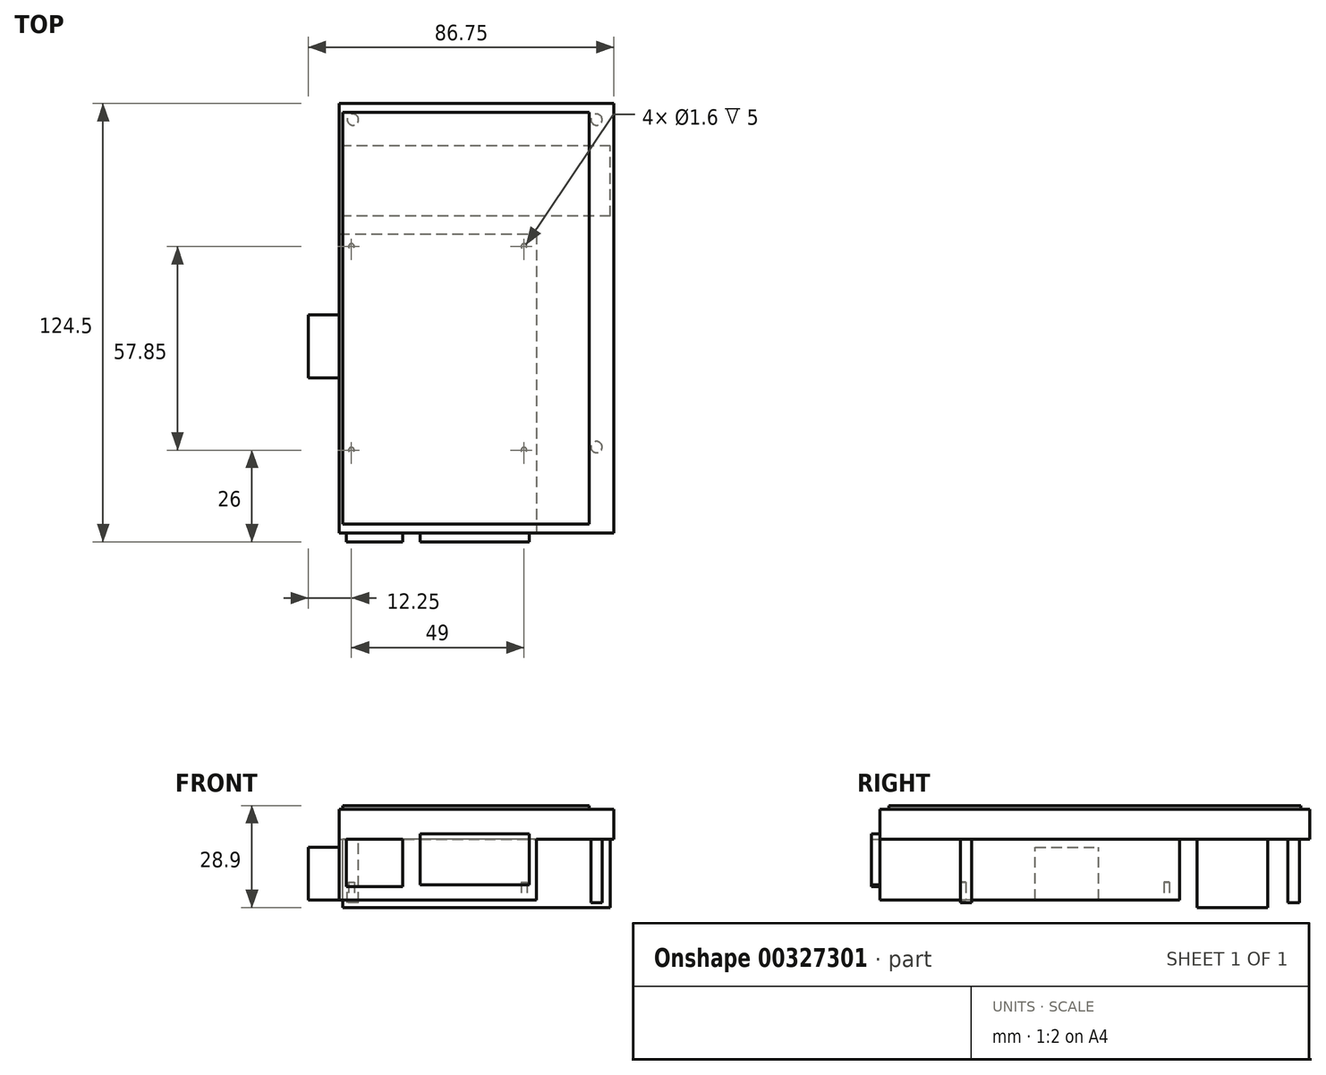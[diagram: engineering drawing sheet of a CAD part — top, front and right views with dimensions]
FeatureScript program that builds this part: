
annotation { "Feature Type Name" : "Feature", "Feature Type Description" : "" }
export const myFeature = defineFeature(function(context is Context, id is Id, definition is map)
    precondition{}
    {
        {
            var Q0;
            Q0=qCreatedBy(makeId("Top.planeOp"),FACE);
            var sketch = newSketch(context, id + "F0", { "sketchPlane" : qUnion([Q0])});
            skLineSegment(sketch, "E0.bottom", {"start": v(-39, -61) * mm, "end": v(39, -61) * mm});
            skLineSegment(sketch, "E0.top", {"start": v(-39, 61) * mm, "end": v(39, 61) * mm});
            skLineSegment(sketch, "E0.left", {"start": v(-39, -61) * mm, "end": v(-39, 61) * mm});
            skLineSegment(sketch, "E0.right", {"start": v(39, -61) * mm, "end": v(39, 61) * mm});
            skPoint(sketch, "E0.middle", {"position": v(0, 0) * mm});
            skSolve(sketch);
        }
        {
            var Q0;
            Q0 = qSketchRegion(id + "F0", true);
            extrude(context, id + "F1", {"entities" : qUnion([Q0]), "depth" : 8.5 * mm});
        }
        {
            var Q0;
            Q0=makeQuery(id+"F1.opExtrude","CAP_FACE",FACE,{"disambiguationData":[OSD([sQuery(id+"F0.wireOp",EDGE,"E0.bottom"),sQuery(id+"F0.wireOp",EDGE,"E0.top"),sQuery(id+"F0.wireOp",EDGE,"E0.left"),sQuery(id+"F0.wireOp",EDGE,"E0.right")])],"isStart":false});
            var sketch = newSketch(context, id + "F2", { "sketchPlane" : qUnion([Q0])});
            skLineSegment(sketch, "E1.bottom", {"start": v(-38, 58.5) * mm, "end": v(32, 58.5) * mm});
            skLineSegment(sketch, "E1.top", {"start": v(-38, -58.5) * mm, "end": v(32, -58.5) * mm});
            skLineSegment(sketch, "E1.left", {"start": v(-38, 58.5) * mm, "end": v(-38, -58.5) * mm});
            skLineSegment(sketch, "E1.right", {"start": v(32, 58.5) * mm, "end": v(32, -58.5) * mm});
            skPoint(sketch, "E1.middle", {"position": v(-3, 0) * mm});
            skPoint(sketch, "E1.middle.positionSnap0", {"position": v(-39, 0) * mm});
            skPoint(sketch, "E1.centerSnap0", {"position": v(-39, 0) * mm});
            skSolve(sketch);
        }
        {
            var Q0;
            Q0 = qSketchRegion(id + "F2", true);
            extrude(context, id + "F3", {"entities" : qUnion([Q0]), "operationType" : NewBodyOperationType.ADD, "depth" : 1 * mm});
        }
        {
            var Q0;
            Q0=makeQuery(id+"F1.opExtrude","CAP_FACE",FACE,{"disambiguationData":[OSD([sQuery(id+"F0.wireOp",EDGE,"E0.bottom"),sQuery(id+"F0.wireOp",EDGE,"E0.top"),sQuery(id+"F0.wireOp",EDGE,"E0.left"),sQuery(id+"F0.wireOp",EDGE,"E0.right")])],"isStart":true});
            var sketch = newSketch(context, id + "F4", { "sketchPlane" : qUnion([Q0])});
            skLineSegment(sketch, "E2.bottom", {"start": v(-39, -24) * mm, "end": v(17, -24) * mm});
            skLineSegment(sketch, "E2.top", {"start": v(-39, 61) * mm, "end": v(17, 61) * mm});
            skLineSegment(sketch, "E2.left", {"start": v(-39, -24) * mm, "end": v(-39, 61) * mm});
            skLineSegment(sketch, "E2.right", {"start": v(17, -24) * mm, "end": v(17, 61) * mm});
            skPoint(sketch, "E2.middle", {"position": v(-11, 18.5) * mm});
            skSolve(sketch);
        }
        {
            var Q0;
            Q0 = qSketchRegion(id + "F4", true);
            extrude(context, id + "F5", {"entities" : qUnion([Q0]), "operationType" : NewBodyOperationType.ADD, "depth" : 17.25 * mm});
        }
        {
            var Q0;
            Q0=makeQuery(id+"F5.boolean.opBoolean","MERGE",FACE,{"derivedFrom":[makeQuery(id+"F1.opExtrude","SWEPT_FACE",FACE,{"disambiguationData":[OSD([sQuery(id+"F0.wireOp",EDGE,"E0.left")])]}),makeQuery(id+"F5.opExtrude","SWEPT_FACE",FACE,{"disambiguationData":[OSD([sQuery(id+"F4.wireOp",EDGE,"E2.left")])]})]});
            var sketch = newSketch(context, id + "F6", { "sketchPlane" : qUnion([Q0])});
            skLineSegment(sketch, "E3.bottom", {"start": v(17, -17.25) * mm, "end": v(-1, -17.25) * mm});
            skLineSegment(sketch, "E3.top", {"start": v(17, -2.25) * mm, "end": v(-1, -2.25) * mm});
            skLineSegment(sketch, "E3.left", {"start": v(17, -17.25) * mm, "end": v(17, -2.25) * mm});
            skLineSegment(sketch, "E3.right", {"start": v(-1, -17.25) * mm, "end": v(-1, -2.25) * mm});
            skSolve(sketch);
        }
        {
            var Q0;
            Q0 = qSketchRegion(id + "F6", true);
            extrude(context, id + "F7", {"entities" : qUnion([Q0]), "operationType" : NewBodyOperationType.ADD, "depth" : 8.75 * mm});
        }
        {
            var Q0;
            Q0=makeQuery(id+"F5.boolean.opBoolean","MERGE",FACE,{"derivedFrom":[makeQuery(id+"F1.opExtrude","SWEPT_FACE",FACE,{"disambiguationData":[OSD([sQuery(id+"F0.wireOp",EDGE,"E0.bottom")])]}),makeQuery(id+"F5.opExtrude","SWEPT_FACE",FACE,{"disambiguationData":[OSD([sQuery(id+"F4.wireOp",EDGE,"E2.top")])]})]});
            var sketch = newSketch(context, id + "F8", { "sketchPlane" : qUnion([Q0])});
            skLineSegment(sketch, "E4.bottom", {"start": v(-36.9, 0) * mm, "end": v(-20.9, 0) * mm});
            skLineSegment(sketch, "E4.top", {"start": v(-36.9, -13.5) * mm, "end": v(-20.9, -13.5) * mm});
            skLineSegment(sketch, "E4.left", {"start": v(-36.9, 0) * mm, "end": v(-36.9, -13.5) * mm});
            skLineSegment(sketch, "E4.right", {"start": v(-20.9, 0) * mm, "end": v(-20.9, -13.5) * mm});
            skPoint(sketch, "E4.middle", {"position": v(-28.9, -6.75) * mm});
            skLineSegment(sketch, "E5.bottom", {"start": v(-16, -13) * mm, "end": v(15, -13) * mm});
            skLineSegment(sketch, "E5.top", {"start": v(-16, 1.5) * mm, "end": v(15, 1.5) * mm});
            skLineSegment(sketch, "E5.left", {"start": v(-16, -13) * mm, "end": v(-16, 1.5) * mm});
            skLineSegment(sketch, "E5.right", {"start": v(15, -13) * mm, "end": v(15, 1.5) * mm});
            skPoint(sketch, "E5.middle", {"position": v(-0.5, -5.75) * mm});
            skSolve(sketch);
        }
        {
            var Q0;
            Q0 = qSketchRegion(id + "F8", true);
            extrude(context, id + "F9", {"entities" : qUnion([Q0]), "operationType" : NewBodyOperationType.ADD, "depth" : 2.5 * mm});
        }
        {
            var Q0;
            Q0=makeQuery(id+"F7.boolean.opBoolean","MERGE",FACE,{"derivedFrom":[makeQuery(id+"F5.opExtrude","CAP_FACE",FACE,{"disambiguationData":[OSD([sQuery(id+"F4.wireOp",EDGE,"E2.bottom"),sQuery(id+"F4.wireOp",EDGE,"E2.top"),sQuery(id+"F4.wireOp",EDGE,"E2.left"),sQuery(id+"F4.wireOp",EDGE,"E2.right")])],"isStart":false}),makeQuery(id+"F7.opExtrude","SWEPT_FACE",FACE,{"disambiguationData":[OSD([sQuery(id+"F6.wireOp",EDGE,"E3.bottom")])]})]});
            var sketch = newSketch(context, id + "F10", { "sketchPlane" : qUnion([Q0])});
            skCircle(sketch, "E6", {"center": v(13.5, 37.5) * mm, "radius": 0.8 * mm});
            skCircle(sketch, "E7", {"center": v(-35.5, 37.5) * mm, "radius": 0.8 * mm});
            skLineSegment(sketch, "E8", {"start": v(-39, 61) * mm, "end": v(-39, 17) * mm, "construction": true});
            skCircle(sketch, "E9.0.1.0", {"center": v(-35.5, -20.35) * mm, "radius": 0.8 * mm});
            skCircle(sketch, "E9.0.1.1", {"center": v(13.5, -20.35) * mm, "radius": 0.8 * mm});
            skLineSegment(sketch, "E9.direction1", {"start": v(-35.5, 37.5) * mm, "end": v(-60.5, 37.5) * mm, "construction": true});
            skLineSegment(sketch, "E9.direction2", {"start": v(-35.5, 37.5) * mm, "end": v(-35.5, -20.35) * mm, "construction": true});
            skSolve(sketch);
        }
        {
            var Q0;
            Q0 = qSketchRegion(id + "F10", true);
            extrude(context, id + "F11", {"entities" : qUnion([Q0]), "operationType" : NewBodyOperationType.REMOVE, "oppositeDirection" : true, "depth" : 5 * mm});
        }
        {
            var Q0;
            Q0=makeQuery(id+"F1.opExtrude","CAP_FACE",FACE,{"disambiguationData":[OSD([sQuery(id+"F0.wireOp",EDGE,"E0.bottom"),sQuery(id+"F0.wireOp",EDGE,"E0.top"),sQuery(id+"F0.wireOp",EDGE,"E0.left"),sQuery(id+"F0.wireOp",EDGE,"E0.right")])],"isStart":true});
            var sketch = newSketch(context, id + "F12", { "sketchPlane" : qUnion([Q0])});
            skCircle(sketch, "E10", {"center": v(-35.1, -56.4) * mm, "radius": 1.6 * mm});
            skCircle(sketch, "E11", {"center": v(34.1, -56.4) * mm, "radius": 1.6 * mm});
            skCircle(sketch, "E12", {"center": v(34.1, 36.6) * mm, "radius": 1.6 * mm});
            skSolve(sketch);
        }
        {
            var Q0;
            Q0 = qSketchRegion(id + "F12", true);
            extrude(context, id + "F13", {"entities" : qUnion([Q0]), "operationType" : NewBodyOperationType.ADD, "depth" : 18 * mm, "offsetDistance" : 25 * mm});
        }
        {
            var Q0;
            Q0=makeQuery(id+"F1.opExtrude","CAP_FACE",FACE,{"disambiguationData":[OSD([sQuery(id+"F0.wireOp",EDGE,"E0.bottom"),sQuery(id+"F0.wireOp",EDGE,"E0.top"),sQuery(id+"F0.wireOp",EDGE,"E0.left"),sQuery(id+"F0.wireOp",EDGE,"E0.right")])],"isStart":true});
            var sketch = newSketch(context, id + "F14", { "sketchPlane" : qUnion([Q0])});
            skLineSegment(sketch, "E13.bottom", {"start": v(38, -29) * mm, "end": v(-38, -29) * mm});
            skLineSegment(sketch, "E13.top", {"start": v(38, -49) * mm, "end": v(-38, -49) * mm});
            skLineSegment(sketch, "E13.left", {"start": v(38, -29) * mm, "end": v(38, -49) * mm});
            skLineSegment(sketch, "E13.right", {"start": v(-38, -29) * mm, "end": v(-38, -49) * mm});
            skPoint(sketch, "E13.middle", {"position": v(0, -39) * mm});
            skPoint(sketch, "E13.middle.positionSnap0", {"position": v(0, -61) * mm});
            skPoint(sketch, "E13.centerSnap0", {"position": v(0, -61) * mm});
            skSolve(sketch);
        }
        {
            var Q0;
            Q0 = qSketchRegion(id + "F14", true);
            extrude(context, id + "F15", {"entities" : qUnion([Q0]), "operationType" : NewBodyOperationType.ADD, "depth" : 19.4 * mm, "offsetDistance" : 25 * mm});
        }
    });
